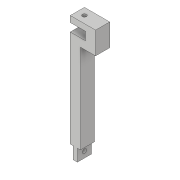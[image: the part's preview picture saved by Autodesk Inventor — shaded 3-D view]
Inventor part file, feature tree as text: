
AUTODESK INVENTOR PART (.ipt)
format: ipt  version: 2019 (Build 230136000, 136)  size: 171,520 bytes
history: native  units: mm
features: extrude x9, sketch x9, thicken_offset x2, projected_geometry x1
ambient origin geometry x8: Origin, YZ Plane, XZ Plane, XY Plane, X Axis, Y Axis, Z Axis, Center Point
bodies: Body1 (feature_tree)
feature tree (21):
  extrude  "Extrusion4"  Depth=5.0mm
  extrude  "Extrusion5"  Depth=3.5mm
  extrude  "Extrusion7"  Depth=2.0mm
  extrude  "Extrusion8"  Depth=5.0mm
  sketch  "Sketch7"  dims[d22=50.0mm d23=0.0mm d29=1.5mm]
  extrude  "Extrusion9"  Depth=1.5mm
  extrude  "Extrusion10"  Depth=6.0mm TaperAngle=0.0deg
  extrude  "Extrusion11"  Depth=3.0mm
  extrude  "Extrusion12"  Depth=10.0mm TaperAngle=0.0deg
  extrude  "Extrusion13"  Depth=4.0mm
  thicken_offset  "Thicken1"
  thicken_offset  "Thicken2"
  sketch  "Sketch1"  dims[d13=4.0mm d14=5.0mm]
  sketch  "Sketch3"  dims[d15=10.0mm d16=3.5mm]
  sketch  "Sketch5"  dims[d17=3.5mm d18=2.0mm]
  sketch  "Sketch6"  dims[d19=3.0mm d20=0.0mm d21=5.0mm]
  sketch  "Sketch9"  dims[d30=1.5mm d31=6.0mm d32=0.0mm]
  sketch  "Sketch10"  dims[d34=2.0mm d35=3.0mm]
  projected_geometry  "Projected Loop1"
  sketch  "Sketch11"  dims[d36=3.5mm d37=10.0mm d38=0.0mm]
  sketch  "Sketch12"  dims[d39=4.05mm d40=4.0mm d41=7.5mm d42=0.0mm d43=5.0mm d44=50.0mm d45=0.0mm d46=20.0mm d47=0.0mm d48=1.5mm d49=1.5mm d50=6.0mm d51=0.0mm d52=2.0mm d53=3.5mm d54=3.0mm d55=6.0mm d56=0.0mm d57=1.0mm d58=1.0mm d59=0.5mm d60=0.5mm]
